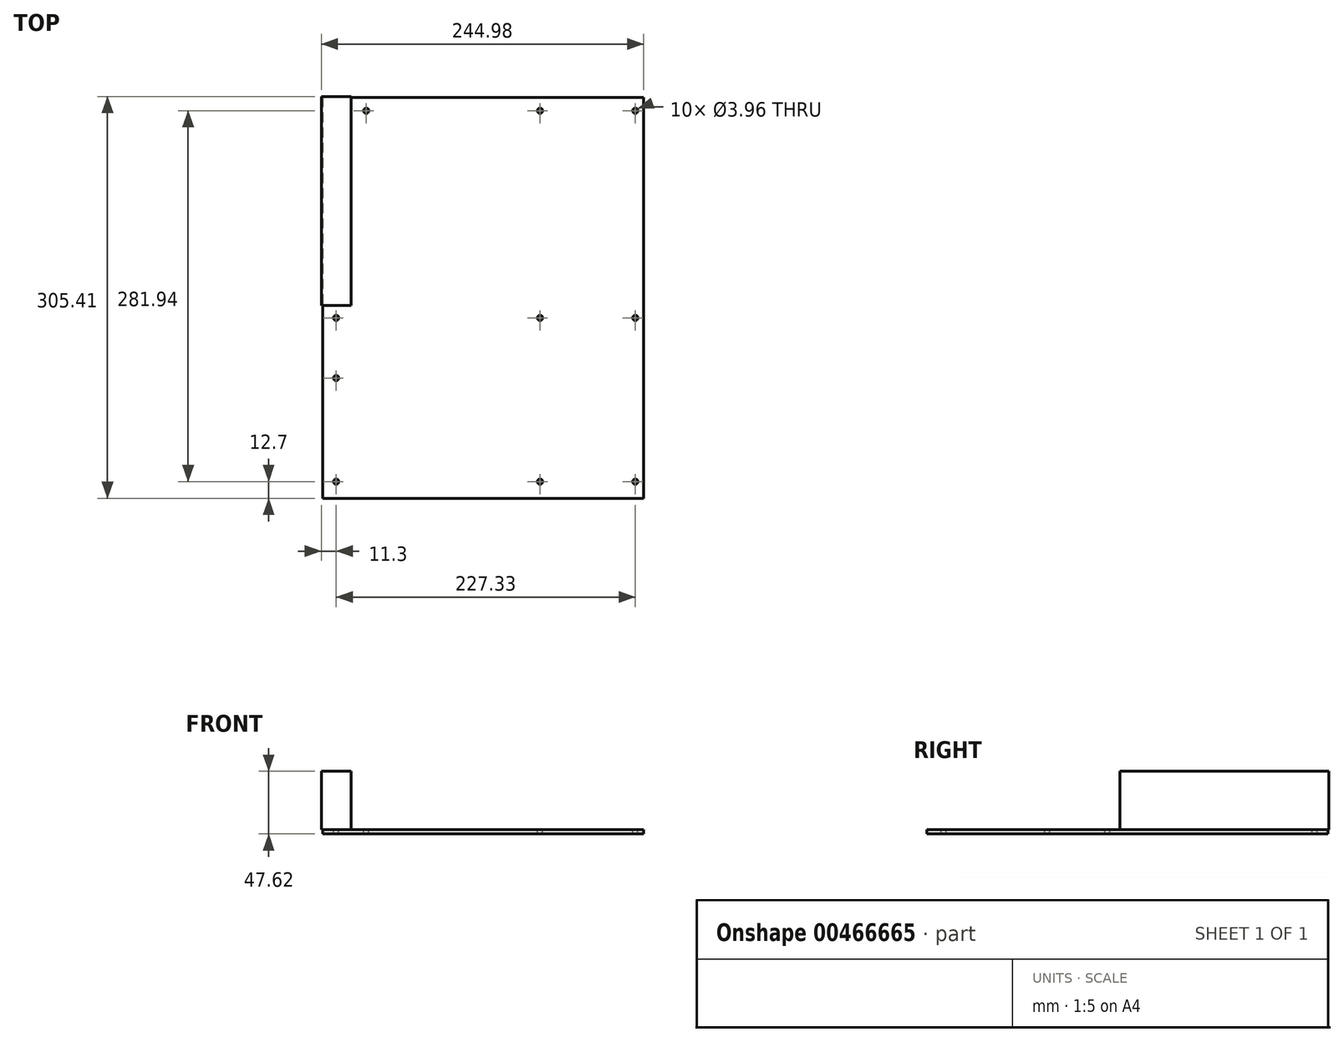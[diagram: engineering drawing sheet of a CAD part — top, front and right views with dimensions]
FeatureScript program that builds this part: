
annotation { "Feature Type Name" : "Feature", "Feature Type Description" : "" }
export const myFeature = defineFeature(function(context is Context, id is Id, definition is map)
    precondition{}
    {
        {
            var Q0;
            Q0=qCreatedBy(makeId("Top.planeOp"),FACE);
            var sketch = newSketch(context, id + "F0", { "sketchPlane" : qUnion([Q0])});
            skLineSegment(sketch, "E0.bottom", {"start": v(0, 0) * mm, "end": v(-243.84, 0) * mm});
            skLineSegment(sketch, "E0.top", {"start": v(0, -304.8) * mm, "end": v(-243.84, -304.8) * mm});
            skLineSegment(sketch, "E0.left", {"start": v(0, 0) * mm, "end": v(0, -304.8) * mm});
            skLineSegment(sketch, "E0.right", {"start": v(-243.84, 0) * mm, "end": v(-243.84, -304.8) * mm});
            skSolve(sketch);
        }
        {
            var Q0;
            Q0 = qSketchRegion(id + "F0", true);
            extrude(context, id + "F1", {"entities" : qUnion([Q0]), "depth" : 3.17 * mm});
        }
        {
            var Q0;
            Q0=makeQuery(id+"F1.opExtrude","CAP_FACE",FACE,{"disambiguationData":[OSD([sQuery(id+"F0.wireOp",EDGE,"E0.bottom"),sQuery(id+"F0.wireOp",EDGE,"E0.top"),sQuery(id+"F0.wireOp",EDGE,"E0.left"),sQuery(id+"F0.wireOp",EDGE,"E0.right")])],"isStart":false});
            var sketch = newSketch(context, id + "F2", { "sketchPlane" : qUnion([Q0])});
            skPoint(sketch, "E1", {"position": v(-210.82, -10.16) * mm});
            skPoint(sketch, "E2", {"position": v(-78.74, -10.16) * mm});
            skPoint(sketch, "E3", {"position": v(-6.35, -10.16) * mm});
            skPoint(sketch, "E4", {"position": v(-233.68, -167.64) * mm});
            skPoint(sketch, "E5", {"position": v(-78.74, -167.64) * mm});
            skPoint(sketch, "E6", {"position": v(-6.35, -167.64) * mm});
            skPoint(sketch, "E7", {"position": v(-233.68, -213.36) * mm});
            skPoint(sketch, "E8", {"position": v(-233.68, -292.1) * mm});
            skPoint(sketch, "E9", {"position": v(-6.35, -292.1) * mm});
            skPoint(sketch, "E10", {"position": v(-78.74, -292.1) * mm});
            skSolve(sketch);
        }
        {
            var Q0;
            Q0=sQuery(id+"F2.wireOp",VERTEX,"E2");
            var Q1;
            Q1=sQuery(id+"F2.wireOp",VERTEX,"E1");
            var Q2;
            Q2=sQuery(id+"F2.wireOp",VERTEX,"E3");
            var Q3;
            Q3=sQuery(id+"F2.wireOp",VERTEX,"E10");
            var Q4;
            Q4=sQuery(id+"F2.wireOp",VERTEX,"E5");
            var Q5;
            Q5=sQuery(id+"F2.wireOp",VERTEX,"E9");
            var Q6;
            Q6=sQuery(id+"F2.wireOp",VERTEX,"E4");
            var Q7;
            Q7=sQuery(id+"F2.wireOp",VERTEX,"E8");
            var Q8;
            Q8=sQuery(id+"F2.wireOp",VERTEX,"E6");
            var Q9;
            Q9=sQuery(id+"F2.wireOp",VERTEX,"E7");
            var Q10;
            Q10=makeQuery(id+"F1.opExtrude","SWEPT_BODY",BODY,{"disambiguationData":[OSD([sQuery(id+"F0.wireOp",EDGE,"E0.bottom"),sQuery(id+"F0.wireOp",EDGE,"E0.top"),sQuery(id+"F0.wireOp",EDGE,"E0.left"),sQuery(id+"F0.wireOp",EDGE,"E0.right")])]});
            hole(context, id + "F3", {"style" : HoleStyle.SIMPLE, "endStyle" : HoleEndStyle.THROUGH, "holeDiameter" : 3.96 * mm, "isTappedThrough" : true, "tappedDepth" : 9.52 * mm, "tapClearance" : 5, "locations" : qUnion([Q0, Q1, Q2, Q3, Q4, Q5, Q6, Q7, Q8, Q9]), "scope" : qUnion([Q10])});
        }
        {
            var Q0;
            Q0=makeQuery(id+"F1.opExtrude","CAP_FACE",FACE,{"disambiguationData":[OSD([sQuery(id+"F0.wireOp",EDGE,"E0.bottom"),sQuery(id+"F0.wireOp",EDGE,"E0.top"),sQuery(id+"F0.wireOp",EDGE,"E0.left"),sQuery(id+"F0.wireOp",EDGE,"E0.right")])],"isStart":false});
            var sketch = newSketch(context, id + "F4", { "sketchPlane" : qUnion([Q0])});
            skLineSegment(sketch, "E11.bottom", {"start": v(-244.98, 0.6) * mm, "end": v(-222.38, 0.6) * mm});
            skLineSegment(sketch, "E11.top", {"start": v(-244.98, -158.14) * mm, "end": v(-222.38, -158.14) * mm});
            skLineSegment(sketch, "E11.left", {"start": v(-244.98, 0.6) * mm, "end": v(-244.98, -158.14) * mm});
            skLineSegment(sketch, "E11.right", {"start": v(-222.38, 0.6) * mm, "end": v(-222.38, -158.14) * mm});
            skPoint(sketch, "E12", {"position": v(-233.68, 0.6) * mm});
            skSolve(sketch);
        }
        {
            var Q0;
            Q0 = qSketchRegion(id + "F4", true);
            extrude(context, id + "F5", {"entities" : qUnion([Q0]), "operationType" : NewBodyOperationType.ADD, "depth" : 44.45 * mm});
        }
    });
